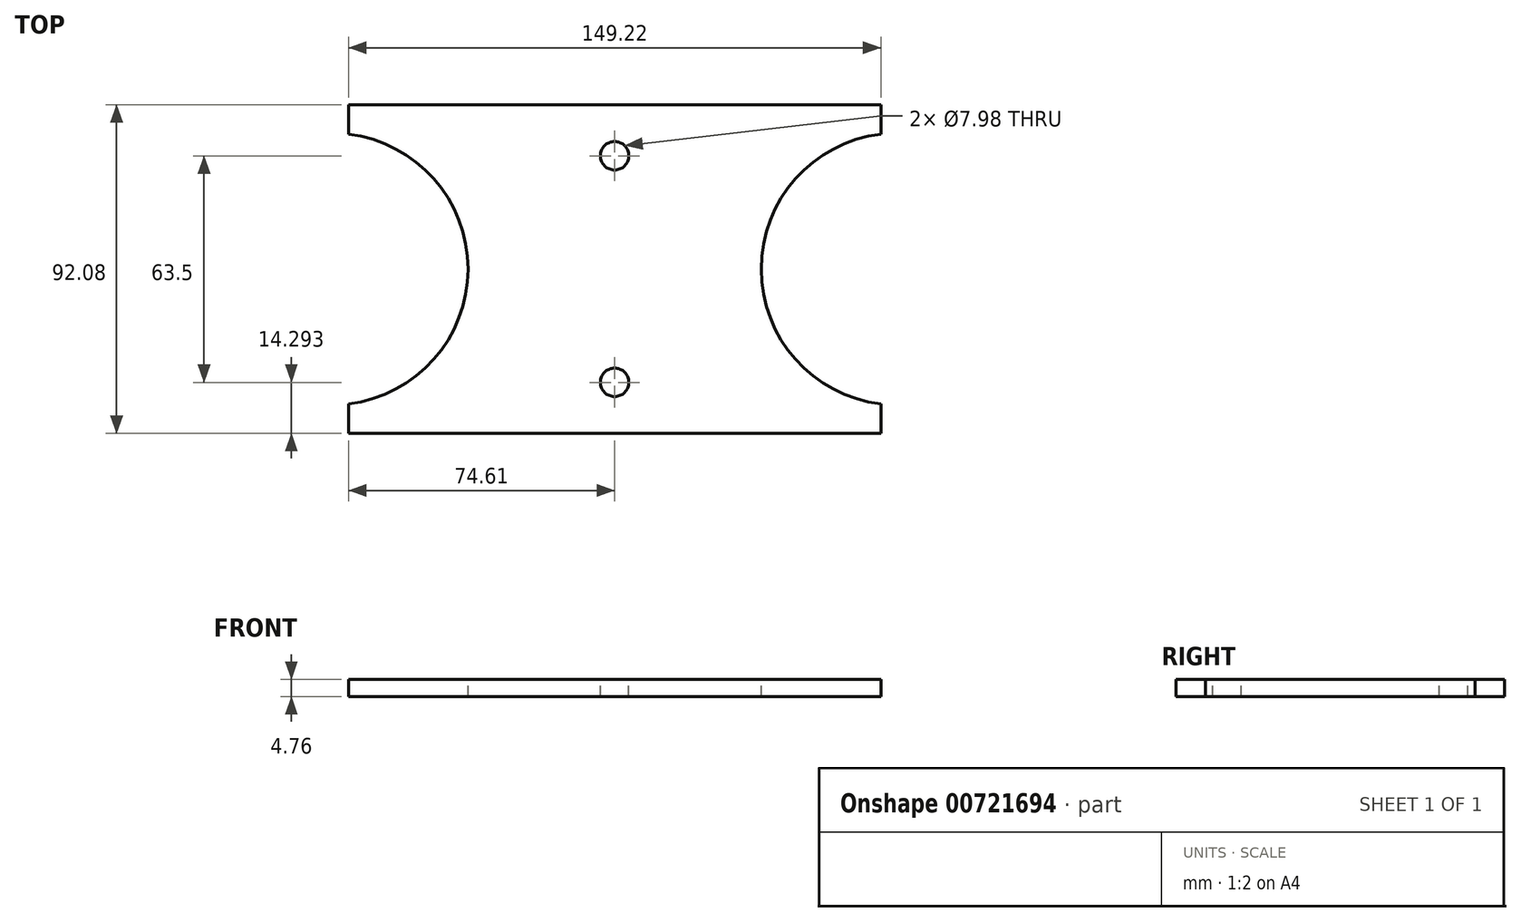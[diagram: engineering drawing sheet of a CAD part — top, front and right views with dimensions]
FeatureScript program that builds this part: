
annotation { "Feature Type Name" : "Feature", "Feature Type Description" : "" }
export const myFeature = defineFeature(function(context is Context, id is Id, definition is map)
    precondition{}
    {
        {
            var Q0;
            Q0=qCreatedBy(makeId("Top.planeOp"),FACE);
            var sketch = newSketch(context, id + "F0", { "sketchPlane" : qUnion([Q0])});
            skLineSegment(sketch, "E0.MirrorCS", {"start": v(19.05, 0) * mm, "end": v(-19.05, 0) * mm});
            skLineSegment(sketch, "E1.MirrorCS", {"start": v(19.05, -92.08) * mm, "end": v(-19.05, -92.08) * mm});
            skLineSegment(sketch, "E2.MirrorCS", {"start": v(19.05, 0) * mm, "end": v(19.05, -92.08) * mm});
            skLineSegment(sketch, "E3.MirrorCS", {"start": v(-19.05, 0) * mm, "end": v(-19.05, -92.08) * mm});
            skSolve(sketch);
        }
        {
            var Q0;
            Q0 = qSketchRegion(id + "F0", true);
            extrude(context, id + "F1", {"entities" : qUnion([Q0]), "oppositeDirection" : true, "depth" : 4.76 * mm, "offsetDistance" : 25.4 * mm});
        }
        {
            var Q0;
            Q0=qCreatedBy(makeId("Top.planeOp"),FACE);
            var sketch = newSketch(context, id + "F2", { "sketchPlane" : qUnion([Q0])});
            skLineSegment(sketch, "E4", {"start": v(0, 0) * mm, "end": v(0, -92.08) * mm, "construction": true});
            skLineSegment(sketch, "E5", {"start": v(-74.61, 0) * mm, "end": v(-74.61, -8.21) * mm});
            skLineSegment(sketch, "E6", {"start": v(-88.36, -46.04) * mm, "end": v(19.05, -46.04) * mm, "construction": true});
            skArc(sketch, "E7", {"start": v(-74.61, -83.86) * mm, "mid": v(-41.08, -46.04) * mm, "end": v(-74.61, -8.21) * mm});
            skLineSegment(sketch, "E8.MirrorCS", {"start": v(-74.61, -92.08) * mm, "end": v(-74.61, -83.86) * mm});
            skLineSegment(sketch, "E9.MirrorCS", {"start": v(74.61, 0) * mm, "end": v(74.61, -8.21) * mm});
            skArc(sketch, "E10.MirrorCS", {"start": v(74.61, -83.86) * mm, "mid": v(41.08, -46.04) * mm, "end": v(74.61, -8.21) * mm});
            skLineSegment(sketch, "E11.MirrorCS", {"start": v(74.61, -92.08) * mm, "end": v(74.61, -83.86) * mm});
            skLineSegment(sketch, "E12", {"start": v(-74.61, 0) * mm, "end": v(-19.05, 0) * mm});
            skLineSegment(sketch, "E13", {"start": v(-19.05, 0) * mm, "end": v(-19.05, -92.08) * mm});
            skLineSegment(sketch, "E14", {"start": v(-19.05, -92.08) * mm, "end": v(-74.61, -92.08) * mm});
            skLineSegment(sketch, "E15", {"start": v(74.61, 0) * mm, "end": v(19.05, 0) * mm});
            skLineSegment(sketch, "E16", {"start": v(74.61, -92.08) * mm, "end": v(19.05, -92.08) * mm});
            skLineSegment(sketch, "E17", {"start": v(19.05, -92.08) * mm, "end": v(19.05, 0) * mm});
            skSolve(sketch);
        }
        {
            var Q0;
            Q0 = qSketchRegion(id + "F2", true);
            extrude(context, id + "F3", {"entities" : qUnion([Q0]), "operationType" : NewBodyOperationType.ADD, "oppositeDirection" : true, "depth" : 4.76 * mm, "offsetDistance" : 25.4 * mm});
        }
        {
            var Q0;
            Q0=qCreatedBy(makeId("Top.planeOp"),FACE);
            var sketch = newSketch(context, id + "F4", { "sketchPlane" : qUnion([Q0])});
            skLineSegment(sketch, "E18", {"start": v(0, 0) * mm, "end": v(0, -92.08) * mm, "construction": true});
            skLineSegment(sketch, "E19", {"start": v(-41.08, -46.04) * mm, "end": v(41.08, -46.04) * mm, "construction": true});
            skCircle(sketch, "E20", {"center": v(0, -14.29) * mm, "radius": 3.99 * mm});
            skCircle(sketch, "E21.MirrorC", {"center": v(0, -77.79) * mm, "radius": 3.99 * mm});
            skSolve(sketch);
        }
        {
            var Q0;
            Q0 = qSketchRegion(id + "F4", true);
            extrude(context, id + "F5", {"entities" : qUnion([Q0]), "operationType" : NewBodyOperationType.REMOVE, "endBound" : BoundingType.THROUGH_ALL, "oppositeDirection" : true, "depth" : 25.4 * mm, "offsetDistance" : 25.4 * mm});
        }
    });
